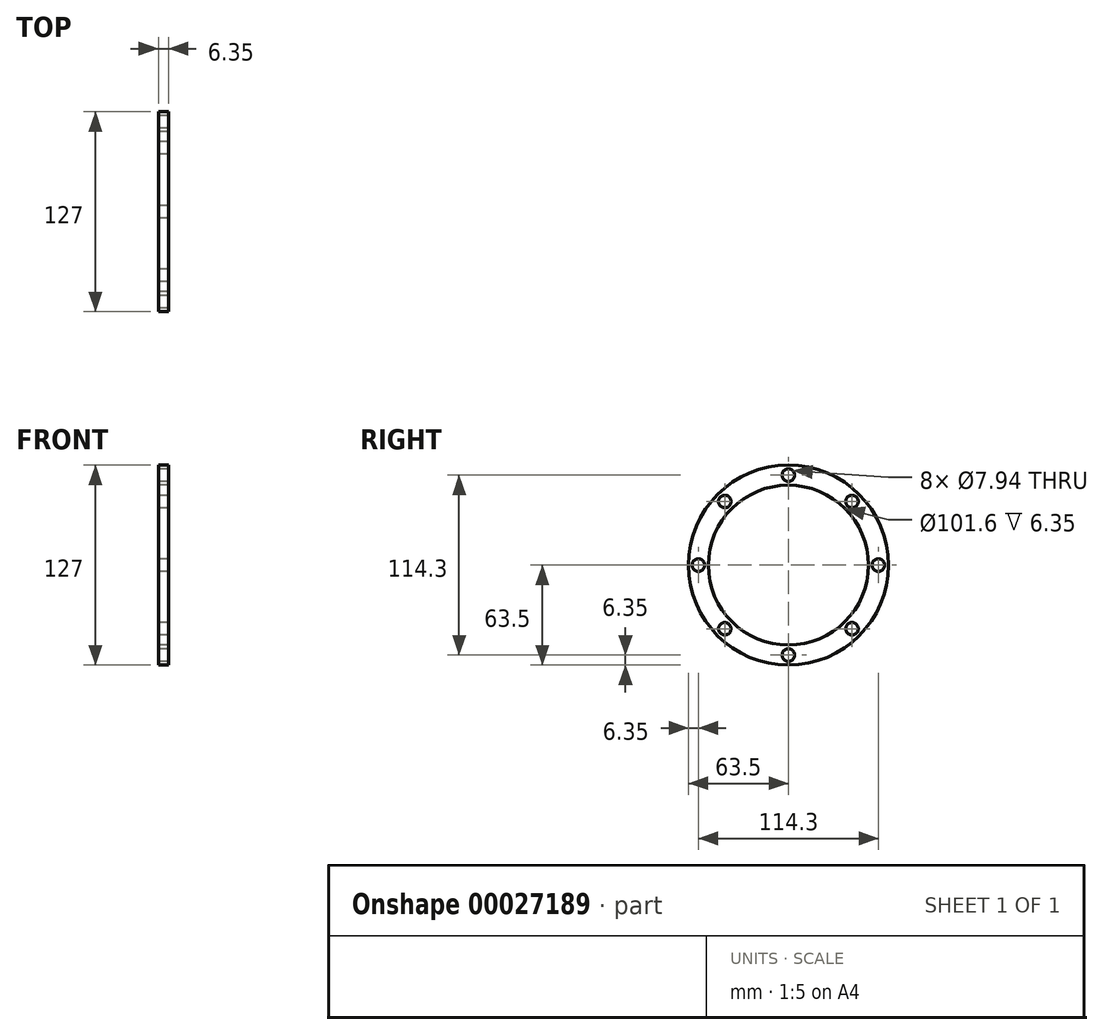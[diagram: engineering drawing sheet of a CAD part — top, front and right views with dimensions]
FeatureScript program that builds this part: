
annotation { "Feature Type Name" : "Feature", "Feature Type Description" : "" }
export const myFeature = defineFeature(function(context is Context, id is Id, definition is map)
    precondition{}
    {
        {
            var Q0;
            Q0=qCreatedBy(makeId("Right.planeOp"),FACE);
            var sketch = newSketch(context, id + "F0", { "sketchPlane" : qUnion([Q0])});
            skCircle(sketch, "E0", {"center": v(0, 0) * mm, "radius": 50.8 * mm});
            skCircle(sketch, "E1", {"center": v(0, 0) * mm, "radius": 63.5 * mm});
            skLineSegment(sketch, "E2", {"start": v(0, 63.5) * mm, "end": v(0, 50.8) * mm});
            skCircle(sketch, "E3", {"center": v(0, 57.15) * mm, "radius": 3.97 * mm});
            skCircle(sketch, "E4.1.0", {"center": v(-40.41, 40.41) * mm, "radius": 3.97 * mm});
            skCircle(sketch, "E4.2.0", {"center": v(-57.15, 0) * mm, "radius": 3.97 * mm});
            skCircle(sketch, "E4.3.0", {"center": v(-40.41, -40.41) * mm, "radius": 3.97 * mm});
            skCircle(sketch, "E4.4.0", {"center": v(0, -57.15) * mm, "radius": 3.97 * mm});
            skCircle(sketch, "E4.5.0", {"center": v(40.41, -40.41) * mm, "radius": 3.97 * mm});
            skCircle(sketch, "E4.6.0", {"center": v(57.15, 0) * mm, "radius": 3.97 * mm});
            skCircle(sketch, "E4.7.0", {"center": v(40.41, 40.41) * mm, "radius": 3.97 * mm});
            skSolve(sketch);
        }
        {
            var Q0;
            Q0=makeQuery(id+"F0.imprint","IMPRINT",FACE,{"disambiguationData":[TD([[makeQuery(id+"F0.imprint","IMPRINT",EDGE,{"derivedFrom":sQuery(id+"F0.wireOp",EDGE,"E0")}),-1.0]])]});
            extrude(context, id + "F1", {"entities" : qUnion([Q0]), "flatOperationType" : FlatOperationType.REMOVE, "offsetDistance" : 25.4 * mm, "depth" : 6.35 * mm, "domain" : OperationDomain.MODEL});
        }
    });
